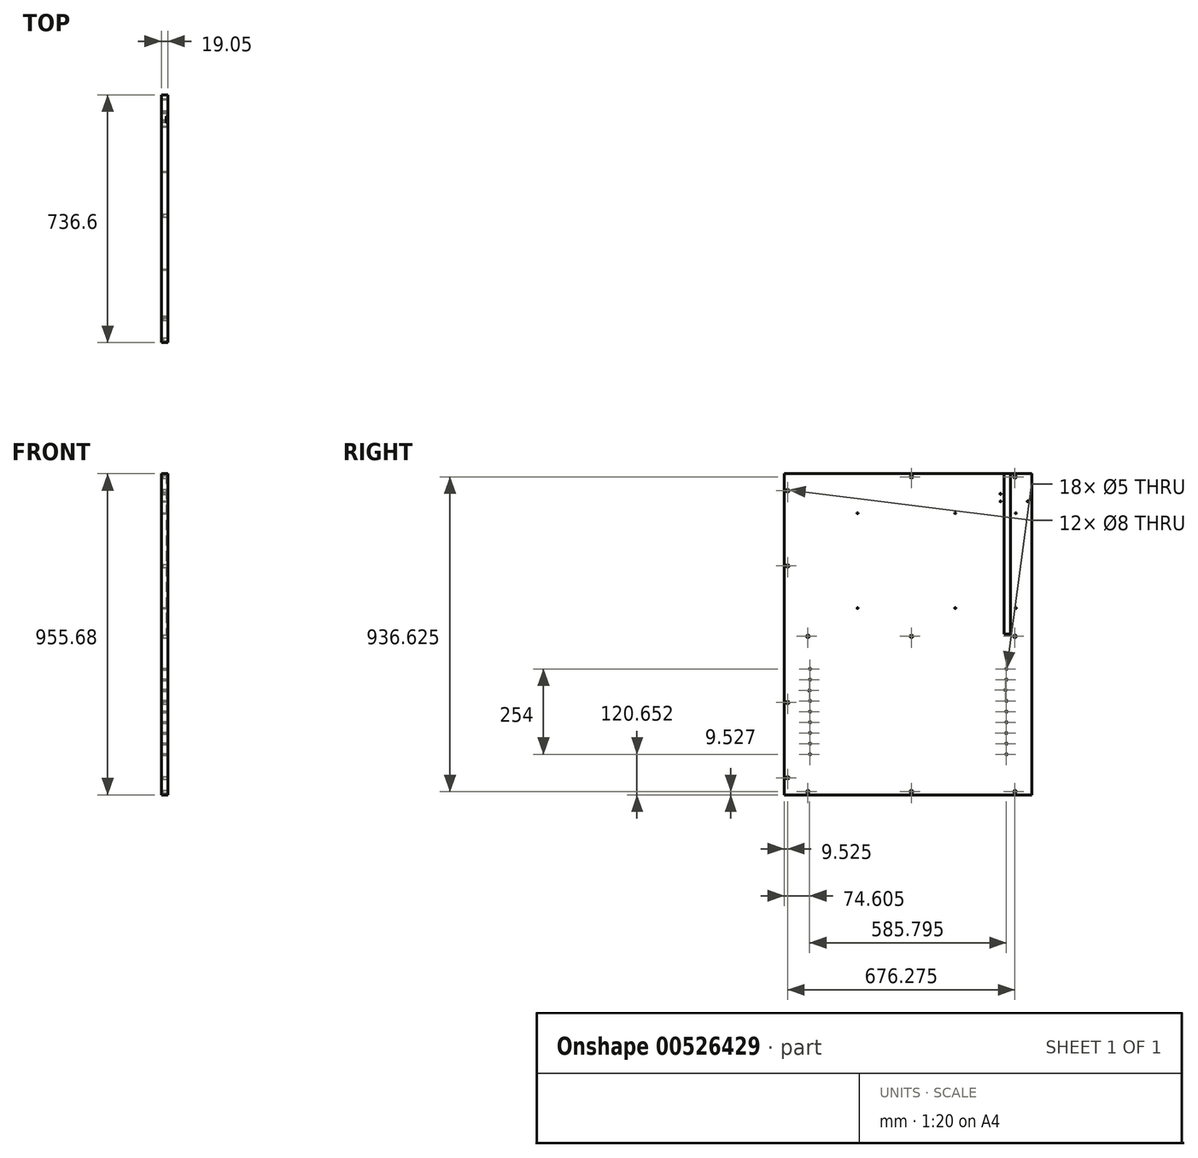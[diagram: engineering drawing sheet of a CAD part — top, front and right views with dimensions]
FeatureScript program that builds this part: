
annotation { "Feature Type Name" : "Feature", "Feature Type Description" : "" }
export const myFeature = defineFeature(function(context is Context, id is Id, definition is map)
    precondition{}
    {
        {
            var Q0;
            Q0=qCreatedBy(makeId("Right.planeOp"),FACE);
            var sketch = newSketch(context, id + "F0", { "sketchPlane" : qUnion([Q0])});
            skLineSegment(sketch, "E0.bottom", {"start": v(368.3, 477.84) * mm, "end": v(-368.3, 477.84) * mm});
            skLineSegment(sketch, "E0.top", {"start": v(368.3, -477.84) * mm, "end": v(-368.3, -477.84) * mm});
            skLineSegment(sketch, "E0.left", {"start": v(368.3, 477.84) * mm, "end": v(368.3, -477.84) * mm});
            skLineSegment(sketch, "E0.right", {"start": v(-368.3, 477.84) * mm, "end": v(-368.3, -477.84) * mm});
            skPoint(sketch, "E0.middle", {"position": v(0, 0) * mm});
            skSolve(sketch);
        }
        {
            var Q0;
            Q0=makeQuery(id+"F0.imprint","IMPRINT",FACE,{"disambiguationData":[TD([[makeQuery(id+"F0.imprint","IMPRINT",EDGE,{"derivedFrom":sQuery(id+"F0.wireOp",EDGE,"E0.bottom")}),1.0]])]});
            extrude(context, id + "F1", {"entities" : qUnion([Q0]), "depth" : 19.05 * mm, "offsetDistance" : 25.4 * mm});
        }
        {
            var Q0;
            Q0=makeQuery(id+"F1.opExtrude","CAP_FACE",FACE,{"disambiguationData":[OSD([sQuery(id+"F0.wireOp",EDGE,"E0.bottom"),sQuery(id+"F0.wireOp",EDGE,"E0.top"),sQuery(id+"F0.wireOp",EDGE,"E0.left"),sQuery(id+"F0.wireOp",EDGE,"E0.right")])],"isStart":false});
            var sketch = newSketch(context, id + "F2", { "sketchPlane" : qUnion([Q0])});
            skLineSegment(sketch, "E1", {"start": v(368.3, 477.84) * mm, "end": v(304.8, 477.84) * mm});
            skLineSegment(sketch, "E2", {"start": v(368.3, 477.84) * mm, "end": v(368.3, 458.79) * mm});
            skLineSegment(sketch, "E3", {"start": v(368.3, 458.79) * mm, "end": v(-368.3, 458.79) * mm});
            skLineSegment(sketch, "E4", {"start": v(368.3, 458.79) * mm, "end": v(368.3, 395.29) * mm});
            skLineSegment(sketch, "E5", {"start": v(368.3, 395.29) * mm, "end": v(266.7, 395.29) * mm});
            skLineSegment(sketch, "E6", {"start": v(368.3, 395.29) * mm, "end": v(355.6, 395.29) * mm});
            skLineSegment(sketch, "E7", {"start": v(355.6, 395.29) * mm, "end": v(274.57, 395.29) * mm});
            skLineSegment(sketch, "E8", {"start": v(274.57, 395.29) * mm, "end": v(274.57, 417.51) * mm});
            skPoint(sketch, "E9", {"position": v(274.57, 417.51) * mm});
            skPoint(sketch, "E10", {"position": v(274.57, 395.29) * mm});
            skPoint(sketch, "E11", {"position": v(355.6, 395.29) * mm});
            skSolve(sketch);
        }
        {
            var Q0;
            Q0=sQuery(id+"F2.wireOp",VERTEX,"E9");
            var Q1;
            Q1=sQuery(id+"F2.wireOp",VERTEX,"E10");
            var Q2;
            Q2=sQuery(id+"F2.wireOp",VERTEX,"E11");
            var Q3;
            Q3=makeQuery(id+"F1.opExtrude","SWEPT_BODY",BODY,{"disambiguationData":[OSD([sQuery(id+"F0.wireOp",EDGE,"E0.bottom"),sQuery(id+"F0.wireOp",EDGE,"E0.top"),sQuery(id+"F0.wireOp",EDGE,"E0.left"),sQuery(id+"F0.wireOp",EDGE,"E0.right")])]});
            hole(context, id + "F3", {"style" : HoleStyle.SIMPLE, "endStyle" : HoleEndStyle.BLIND, "holeDiameter" : 3.17 * mm, "holeDepth" : 14.22 * mm, "isTappedThrough" : true, "tappedDepth" : 12.7 * mm, "tapClearance" : 3, "startFromSketch" : true, "locations" : qUnion([Q0, Q1, Q2]), "scope" : qUnion([Q3])});
        }
        {
            var Q0;
            Q0=makeQuery(id+"F1.opExtrude","CAP_FACE",FACE,{"disambiguationData":[OSD([sQuery(id+"F0.wireOp",EDGE,"E0.bottom"),sQuery(id+"F0.wireOp",EDGE,"E0.top"),sQuery(id+"F0.wireOp",EDGE,"E0.left"),sQuery(id+"F0.wireOp",EDGE,"E0.right")])],"isStart":false});
            var sketch = newSketch(context, id + "F4", { "sketchPlane" : qUnion([Q0])});
            skLineSegment(sketch, "E12", {"start": v(368.3, 477.84) * mm, "end": v(368.3, 468.31) * mm});
            skLineSegment(sketch, "E13", {"start": v(368.3, 468.31) * mm, "end": v(-368.3, 468.31) * mm});
            skLineSegment(sketch, "E14", {"start": v(-368.3, 477.84) * mm, "end": v(-349.25, 477.84) * mm});
            skLineSegment(sketch, "E15", {"start": v(-349.25, 477.84) * mm, "end": v(-349.25, -477.84) * mm});
            skLineSegment(sketch, "E16", {"start": v(-368.3, -477.84) * mm, "end": v(-368.3, -468.31) * mm});
            skLineSegment(sketch, "E17", {"start": v(-368.3, -468.31) * mm, "end": v(368.3, -468.31) * mm});
            skLineSegment(sketch, "E18", {"start": v(-368.3, -477.84) * mm, "end": v(-358.77, -477.84) * mm});
            skLineSegment(sketch, "E19", {"start": v(-358.77, -477.84) * mm, "end": v(-358.78, 477.84) * mm});
            skLineSegment(sketch, "E20", {"start": v(-368.3, 468.31) * mm, "end": v(-298.45, 468.31) * mm});
            skLineSegment(sketch, "E21", {"start": v(-368.3, -468.31) * mm, "end": v(-298.45, -468.31) * mm});
            skLineSegment(sketch, "E22", {"start": v(368.3, -468.31) * mm, "end": v(317.5, -468.31) * mm});
            skLineSegment(sketch, "E23", {"start": v(368.3, -468.31) * mm, "end": v(9.53, -468.31) * mm});
            skLineSegment(sketch, "E24", {"start": v(-358.78, 477.84) * mm, "end": v(-358.78, 427.04) * mm});
            skLineSegment(sketch, "E25", {"start": v(-358.77, -477.84) * mm, "end": v(-358.77, -427.04) * mm});
            skPoint(sketch, "E26", {"position": v(-358.78, 427.04) * mm});
            skPoint(sketch, "E27", {"position": v(317.5, -468.31) * mm});
            skPoint(sketch, "E28", {"position": v(9.53, -468.31) * mm});
            skPoint(sketch, "E29", {"position": v(-298.45, -468.31) * mm});
            skPoint(sketch, "E30", {"position": v(-358.77, -427.04) * mm});
            skPoint(sketch, "E31", {"position": v(-358.78, 0) * mm});
            skLineSegment(sketch, "E32", {"start": v(-368.3, 468.31) * mm, "end": v(-368.3, 477.84) * mm});
            skLineSegment(sketch, "E33", {"start": v(368.3, 468.31) * mm, "end": v(317.5, 468.31) * mm});
            skLineSegment(sketch, "E34", {"start": v(317.5, 468.31) * mm, "end": v(9.52, 468.31) * mm});
            skLineSegment(sketch, "E35", {"start": v(-358.78, 0) * mm, "end": v(-358.78, 203.2) * mm});
            skLineSegment(sketch, "E36", {"start": v(-358.78, 203.2) * mm, "end": v(-358.77, -203.2) * mm});
            skPoint(sketch, "E37", {"position": v(-358.78, 203.2) * mm});
            skPoint(sketch, "E38", {"position": v(-358.77, -203.2) * mm});
            skSolve(sketch);
        }
        {
            var Q0;
            Q0=sQuery(id+"F4.wireOp",VERTEX,"E20.end");
            var Q1;
            Q1=sQuery(id+"F4.wireOp",VERTEX,"E34.end");
            var Q2;
            Q2=sQuery(id+"F4.wireOp",VERTEX,"E34.start");
            var Q3;
            Q3=sQuery(id+"F4.wireOp",VERTEX,"E26");
            var Q4;
            Q4=sQuery(id+"F4.wireOp",VERTEX,"E30");
            var Q5;
            Q5=sQuery(id+"F4.wireOp",VERTEX,"E29");
            var Q6;
            Q6=sQuery(id+"F4.wireOp",VERTEX,"E28");
            var Q7;
            Q7=sQuery(id+"F4.wireOp",VERTEX,"E27");
            var Q8;
            Q8=sQuery(id+"F4.wireOp",VERTEX,"E37");
            var Q9;
            Q9=sQuery(id+"F4.wireOp",VERTEX,"E38");
            var Q10;
            Q10=makeQuery(id+"F1.opExtrude","SWEPT_BODY",BODY,{"disambiguationData":[OSD([sQuery(id+"F0.wireOp",EDGE,"E0.bottom"),sQuery(id+"F0.wireOp",EDGE,"E0.top"),sQuery(id+"F0.wireOp",EDGE,"E0.left"),sQuery(id+"F0.wireOp",EDGE,"E0.right")])]});
            hole(context, id + "F5", {"style" : HoleStyle.SIMPLE, "endStyle" : HoleEndStyle.BLIND, "holeDiameter" : 8 * mm, "holeDepth" : 14.22 * mm, "isTappedThrough" : true, "tappedDepth" : 12.7 * mm, "tapClearance" : 3, "startFromSketch" : true, "locations" : qUnion([Q0, Q1, Q2, Q3, Q4, Q5, Q6, Q7, Q8, Q9]), "scope" : qUnion([Q10])});
        }
        {
            var Q0;
            Q0=makeQuery(id+"F1.opExtrude","CAP_FACE",FACE,{"disambiguationData":[OSD([sQuery(id+"F0.wireOp",EDGE,"E0.bottom"),sQuery(id+"F0.wireOp",EDGE,"E0.top"),sQuery(id+"F0.wireOp",EDGE,"E0.left"),sQuery(id+"F0.wireOp",EDGE,"E0.right")])],"isStart":false});
            var sketch = newSketch(context, id + "F6", { "sketchPlane" : qUnion([Q0])});
            skLineSegment(sketch, "E39", {"start": v(368.3, 477.84) * mm, "end": v(368.3, 363.54) * mm});
            skLineSegment(sketch, "E40", {"start": v(368.3, 477.84) * mm, "end": v(368.3, 458.79) * mm});
            skLineSegment(sketch, "E41", {"start": v(368.3, 458.79) * mm, "end": v(368.3, 360.24) * mm});
            skLineSegment(sketch, "E42", {"start": v(368.3, 360.24) * mm, "end": v(-241.3, 360.24) * mm});
            skLineSegment(sketch, "E43", {"start": v(368.3, 360.24) * mm, "end": v(320.04, 360.24) * mm});
            skLineSegment(sketch, "E44", {"start": v(368.3, 360.24) * mm, "end": v(139.7, 360.24) * mm});
            skLineSegment(sketch, "E45", {"start": v(368.3, 360.24) * mm, "end": v(-150.88, 360.24) * mm});
            skPoint(sketch, "E46", {"position": v(320.04, 360.24) * mm});
            skPoint(sketch, "E47", {"position": v(139.7, 360.24) * mm});
            skPoint(sketch, "E48", {"position": v(-150.88, 360.24) * mm});
            skLineSegment(sketch, "E49", {"start": v(368.3, 477.84) * mm, "end": v(368.3, 468.31) * mm});
            skLineSegment(sketch, "E50", {"start": v(368.3, 468.31) * mm, "end": v(387.35, 468.31) * mm});
            skLineSegment(sketch, "E51", {"start": v(387.35, 468.31) * mm, "end": v(387.35, 303.21) * mm});
            skLineSegment(sketch, "E52", {"start": v(387.35, 303.21) * mm, "end": v(368.3, 303.21) * mm});
            skLineSegment(sketch, "E53", {"start": v(368.3, 303.21) * mm, "end": v(368.3, 300.04) * mm});
            skLineSegment(sketch, "E54", {"start": v(368.3, 300.04) * mm, "end": v(387.35, 300.04) * mm});
            skLineSegment(sketch, "E55", {"start": v(387.35, 300.04) * mm, "end": v(387.35, 0) * mm});
            skLineSegment(sketch, "E56", {"start": v(387.35, 300.04) * mm, "end": v(387.35, -4.76) * mm});
            skLineSegment(sketch, "E57", {"start": v(387.35, -4.76) * mm, "end": v(368.3, -4.76) * mm});
            skLineSegment(sketch, "E58", {"start": v(368.3, -4.76) * mm, "end": v(368.3, -7.94) * mm});
            skLineSegment(sketch, "E59", {"start": v(368.3, -7.94) * mm, "end": v(387.35, -7.94) * mm});
            skLineSegment(sketch, "E60", {"start": v(387.35, -7.94) * mm, "end": v(387.35, -477.84) * mm});
            skLineSegment(sketch, "E61", {"start": v(387.35, -477.84) * mm, "end": v(368.3, -477.84) * mm});
            skLineSegment(sketch, "E62", {"start": v(387.35, 147.64) * mm, "end": v(387.35, 280.99) * mm});
            skLineSegment(sketch, "E63", {"start": v(387.35, 280.99) * mm, "end": v(311.15, 280.99) * mm});
            skLineSegment(sketch, "E64", {"start": v(311.15, 280.99) * mm, "end": v(311.15, 14.29) * mm});
            skLineSegment(sketch, "E65", {"start": v(311.15, 14.29) * mm, "end": v(387.35, 14.29) * mm});
            skLineSegment(sketch, "E66", {"start": v(368.3, 14.29) * mm, "end": v(368.3, 77.79) * mm});
            skLineSegment(sketch, "E67", {"start": v(368.3, 77.79) * mm, "end": v(-241.3, 77.79) * mm});
            skLineSegment(sketch, "E68", {"start": v(368.3, 77.79) * mm, "end": v(320.04, 77.79) * mm});
            skLineSegment(sketch, "E69", {"start": v(368.3, 77.79) * mm, "end": v(-150.88, 77.79) * mm});
            skLineSegment(sketch, "E70", {"start": v(368.3, 77.79) * mm, "end": v(139.7, 77.79) * mm});
            skPoint(sketch, "E71", {"position": v(139.7, 77.79) * mm});
            skPoint(sketch, "E72", {"position": v(-150.88, 77.79) * mm});
            skPoint(sketch, "E73", {"position": v(320.04, 77.79) * mm});
            skLineSegment(sketch, "E74", {"start": v(368.3, -6.35) * mm, "end": v(-368.3, -6.35) * mm});
            skLineSegment(sketch, "E75", {"start": v(-368.3, -6.35) * mm, "end": v(-298.45, -6.35) * mm});
            skLineSegment(sketch, "E76", {"start": v(368.3, -6.35) * mm, "end": v(317.5, -6.35) * mm});
            skLineSegment(sketch, "E77", {"start": v(368.3, -6.35) * mm, "end": v(9.52, -6.35) * mm});
            skPoint(sketch, "E78", {"position": v(317.5, -6.35) * mm});
            skPoint(sketch, "E79", {"position": v(9.52, -6.35) * mm});
            skPoint(sketch, "E80", {"position": v(-298.45, -6.35) * mm});
            skSolve(sketch);
        }
        {
            var Q0;
            Q0=sQuery(id+"F6.wireOp",VERTEX,"E48");
            var Q1;
            Q1=sQuery(id+"F6.wireOp",VERTEX,"E47");
            var Q2;
            Q2=sQuery(id+"F6.wireOp",VERTEX,"E46");
            var Q3;
            Q3=sQuery(id+"F6.wireOp",VERTEX,"E73");
            var Q4;
            Q4=sQuery(id+"F6.wireOp",VERTEX,"E71");
            var Q5;
            Q5=sQuery(id+"F6.wireOp",VERTEX,"E72");
            var Q6;
            Q6=makeQuery(id+"F1.opExtrude","SWEPT_BODY",BODY,{"disambiguationData":[OSD([sQuery(id+"F0.wireOp",EDGE,"E0.bottom"),sQuery(id+"F0.wireOp",EDGE,"E0.top"),sQuery(id+"F0.wireOp",EDGE,"E0.left"),sQuery(id+"F0.wireOp",EDGE,"E0.right")])]});
            hole(context, id + "F7", {"style" : HoleStyle.SIMPLE, "endStyle" : HoleEndStyle.BLIND, "holeDiameter" : 3.17 * mm, "holeDepth" : 14.22 * mm, "isTappedThrough" : true, "tappedDepth" : 12.7 * mm, "tapClearance" : 3, "startFromSketch" : true, "locations" : qUnion([Q0, Q1, Q2, Q3, Q4, Q5]), "scope" : qUnion([Q6])});
        }
        {
            var Q0;
            Q0=sQuery(id+"F6.wireOp",VERTEX,"E80");
            var Q1;
            Q1=sQuery(id+"F6.wireOp",VERTEX,"E79");
            var Q2;
            Q2=sQuery(id+"F6.wireOp",VERTEX,"E78");
            var Q3;
            Q3=makeQuery(id+"F1.opExtrude","SWEPT_BODY",BODY,{"disambiguationData":[OSD([sQuery(id+"F0.wireOp",EDGE,"E0.bottom"),sQuery(id+"F0.wireOp",EDGE,"E0.top"),sQuery(id+"F0.wireOp",EDGE,"E0.left"),sQuery(id+"F0.wireOp",EDGE,"E0.right")])]});
            hole(context, id + "F8", {"style" : HoleStyle.SIMPLE, "endStyle" : HoleEndStyle.BLIND, "holeDiameter" : 8 * mm, "holeDepth" : 14.22 * mm, "isTappedThrough" : true, "tappedDepth" : 12.7 * mm, "tapClearance" : 3, "startFromSketch" : true, "locations" : qUnion([Q0, Q1, Q2]), "scope" : qUnion([Q3])});
        }
        {
            var Q0;
            Q0=makeQuery(id+"F1.opExtrude","CAP_FACE",FACE,{"disambiguationData":[OSD([sQuery(id+"F0.wireOp",EDGE,"E0.bottom"),sQuery(id+"F0.wireOp",EDGE,"E0.top"),sQuery(id+"F0.wireOp",EDGE,"E0.left"),sQuery(id+"F0.wireOp",EDGE,"E0.right")])],"isStart":false});
            var sketch = newSketch(context, id + "F9", { "sketchPlane" : qUnion([Q0])});
            skLineSegment(sketch, "E81", {"start": v(368.3, 477.84) * mm, "end": v(304.8, 477.84) * mm});
            skLineSegment(sketch, "E82", {"start": v(304.8, 477.84) * mm, "end": v(285.75, 477.84) * mm});
            skLineSegment(sketch, "E83", {"start": v(285.75, 477.84) * mm, "end": v(285.75, 0) * mm});
            skLineSegment(sketch, "E84", {"start": v(285.75, 0) * mm, "end": v(304.8, 0) * mm});
            skLineSegment(sketch, "E85", {"start": v(304.8, 0) * mm, "end": v(304.8, 477.84) * mm});
            skSolve(sketch);
        }
        {
            var Q0;
            Q0=makeQuery(id+"F9.imprint","IMPRINT",FACE,{"disambiguationData":[TD([[makeQuery(id+"F9.imprint","IMPRINT",EDGE,{"derivedFrom":sQuery(id+"F9.wireOp",EDGE,"E82")}),1.0]])]});
            extrude(context, id + "F10", {"entities" : qUnion([Q0]), "operationType" : NewBodyOperationType.REMOVE, "oppositeDirection" : true, "depth" : 4.83 * mm, "offsetDistance" : 25.4 * mm});
        }
        {
            var Q0;
            Q0=makeQuery(id+"F1.opExtrude","CAP_FACE",FACE,{"disambiguationData":[OSD([sQuery(id+"F0.wireOp",EDGE,"E0.bottom"),sQuery(id+"F0.wireOp",EDGE,"E0.top"),sQuery(id+"F0.wireOp",EDGE,"E0.left"),sQuery(id+"F0.wireOp",EDGE,"E0.right")])],"isStart":false});
            var sketch = newSketch(context, id + "F11", { "sketchPlane" : qUnion([Q0])});
            skLineSegment(sketch, "E86", {"start": v(368.3, -477.84) * mm, "end": v(292.1, -477.84) * mm});
            skLineSegment(sketch, "E87", {"start": v(292.1, -477.84) * mm, "end": v(292.1, -46.04) * mm});
            skLineSegment(sketch, "E88", {"start": v(-368.3, -477.84) * mm, "end": v(-292.1, -477.84) * mm});
            skLineSegment(sketch, "E89", {"start": v(-292.1, -477.84) * mm, "end": v(-292.1, -46.04) * mm});
            skLineSegment(sketch, "E90", {"start": v(292.1, -477.84) * mm, "end": v(292.1, -325.44) * mm});
            skLineSegment(sketch, "E91", {"start": v(-292.1, -477.84) * mm, "end": v(-292.1, -325.44) * mm});
            skLineSegment(sketch, "E92", {"start": v(-292.1, -325.44) * mm, "end": v(-292.1, -293.69) * mm});
            skLineSegment(sketch, "E93", {"start": v(-292.1, -293.69) * mm, "end": v(-292.1, -261.94) * mm});
            skLineSegment(sketch, "E94", {"start": v(-292.1, -261.94) * mm, "end": v(-292.1, -230.19) * mm});
            skLineSegment(sketch, "E95", {"start": v(-292.1, -230.19) * mm, "end": v(-292.1, -198.44) * mm});
            skLineSegment(sketch, "E96", {"start": v(-292.1, -198.44) * mm, "end": v(-292.1, -166.69) * mm});
            skLineSegment(sketch, "E97", {"start": v(-292.1, -166.69) * mm, "end": v(-292.1, -134.94) * mm});
            skLineSegment(sketch, "E98", {"start": v(-292.1, -134.94) * mm, "end": v(-292.1, -103.19) * mm});
            skLineSegment(sketch, "E99", {"start": v(-292.1, -325.44) * mm, "end": v(-292.1, -357.19) * mm});
            skLineSegment(sketch, "E100", {"start": v(-292.1, -357.19) * mm, "end": v(-292.1, -477.84) * mm});
            skLineSegment(sketch, "E101", {"start": v(292.1, -477.84) * mm, "end": v(292.1, -357.19) * mm});
            skLineSegment(sketch, "E102", {"start": v(292.1, -325.44) * mm, "end": v(292.1, -293.69) * mm});
            skLineSegment(sketch, "E103", {"start": v(292.1, -293.69) * mm, "end": v(292.1, -261.94) * mm});
            skLineSegment(sketch, "E104", {"start": v(292.1, -261.94) * mm, "end": v(292.1, -230.19) * mm});
            skLineSegment(sketch, "E105", {"start": v(292.1, -230.19) * mm, "end": v(292.1, -198.44) * mm});
            skLineSegment(sketch, "E106", {"start": v(292.1, -198.44) * mm, "end": v(292.1, -166.69) * mm});
            skLineSegment(sketch, "E107", {"start": v(292.1, -166.69) * mm, "end": v(292.1, -134.94) * mm});
            skLineSegment(sketch, "E108", {"start": v(292.1, -134.94) * mm, "end": v(292.1, -103.19) * mm});
            skPoint(sketch, "E109", {"position": v(-292.1, -103.19) * mm});
            skPoint(sketch, "E110", {"position": v(-292.1, -134.94) * mm});
            skPoint(sketch, "E111", {"position": v(-293.7, -167.67) * mm});
            skPoint(sketch, "E112", {"position": v(-292.1, -198.44) * mm});
            skPoint(sketch, "E113", {"position": v(-292.1, -230.19) * mm});
            skPoint(sketch, "E114", {"position": v(-292.1, -261.94) * mm});
            skPoint(sketch, "E115", {"position": v(-292.1, -293.69) * mm});
            skPoint(sketch, "E116", {"position": v(-292.1, -325.44) * mm});
            skPoint(sketch, "E117", {"position": v(-292.1, -357.19) * mm});
            skPoint(sketch, "E118", {"position": v(292.1, -357.19) * mm});
            skPoint(sketch, "E119", {"position": v(292.1, -325.44) * mm});
            skPoint(sketch, "E120", {"position": v(291.52, -294.05) * mm});
            skPoint(sketch, "E121", {"position": v(292.1, -261.94) * mm});
            skPoint(sketch, "E122", {"position": v(292.1, -230.19) * mm});
            skPoint(sketch, "E123", {"position": v(292.1, -198.44) * mm});
            skPoint(sketch, "E124", {"position": v(289.58, -165.73) * mm});
            skPoint(sketch, "E125", {"position": v(292.1, -134.94) * mm});
            skPoint(sketch, "E126", {"position": v(292.1, -103.19) * mm});
            skSolve(sketch);
        }
        {
            var Q0;
            Q0=sQuery(id+"F11.wireOp",VERTEX,"E109");
            var Q1;
            Q1=sQuery(id+"F11.wireOp",VERTEX,"E110");
            var Q2;
            Q2=sQuery(id+"F11.wireOp",VERTEX,"E111");
            var Q3;
            Q3=sQuery(id+"F11.wireOp",VERTEX,"E112");
            var Q4;
            Q4=sQuery(id+"F11.wireOp",VERTEX,"E113");
            var Q5;
            Q5=sQuery(id+"F11.wireOp",VERTEX,"E114");
            var Q6;
            Q6=sQuery(id+"F11.wireOp",VERTEX,"E115");
            var Q7;
            Q7=sQuery(id+"F11.wireOp",VERTEX,"E116");
            var Q8;
            Q8=sQuery(id+"F11.wireOp",VERTEX,"E117");
            var Q9;
            Q9=sQuery(id+"F11.wireOp",VERTEX,"E118");
            var Q10;
            Q10=sQuery(id+"F11.wireOp",VERTEX,"E119");
            var Q11;
            Q11=sQuery(id+"F11.wireOp",VERTEX,"E120");
            var Q12;
            Q12=sQuery(id+"F11.wireOp",VERTEX,"E121");
            var Q13;
            Q13=sQuery(id+"F11.wireOp",VERTEX,"E122");
            var Q14;
            Q14=sQuery(id+"F11.wireOp",VERTEX,"E123");
            var Q15;
            Q15=sQuery(id+"F11.wireOp",VERTEX,"E124");
            var Q16;
            Q16=sQuery(id+"F11.wireOp",VERTEX,"E125");
            var Q17;
            Q17=sQuery(id+"F11.wireOp",VERTEX,"E126");
            var Q18;
            Q18=makeQuery(id+"F1.opExtrude","SWEPT_BODY",BODY,{"disambiguationData":[OSD([sQuery(id+"F0.wireOp",EDGE,"E0.bottom"),sQuery(id+"F0.wireOp",EDGE,"E0.top"),sQuery(id+"F0.wireOp",EDGE,"E0.left"),sQuery(id+"F0.wireOp",EDGE,"E0.right")])]});
            hole(context, id + "F12", {"style" : HoleStyle.SIMPLE, "endStyle" : HoleEndStyle.BLIND, "holeDiameter" : 5 * mm, "holeDepth" : 14.22 * mm, "isTappedThrough" : true, "tappedDepth" : 12.7 * mm, "tapClearance" : 3, "startFromSketch" : true, "locations" : qUnion([Q0, Q1, Q2, Q3, Q4, Q5, Q6, Q7, Q8, Q9, Q10, Q11, Q12, Q13, Q14, Q15, Q16, Q17]), "scope" : qUnion([Q18])});
        }
    });
